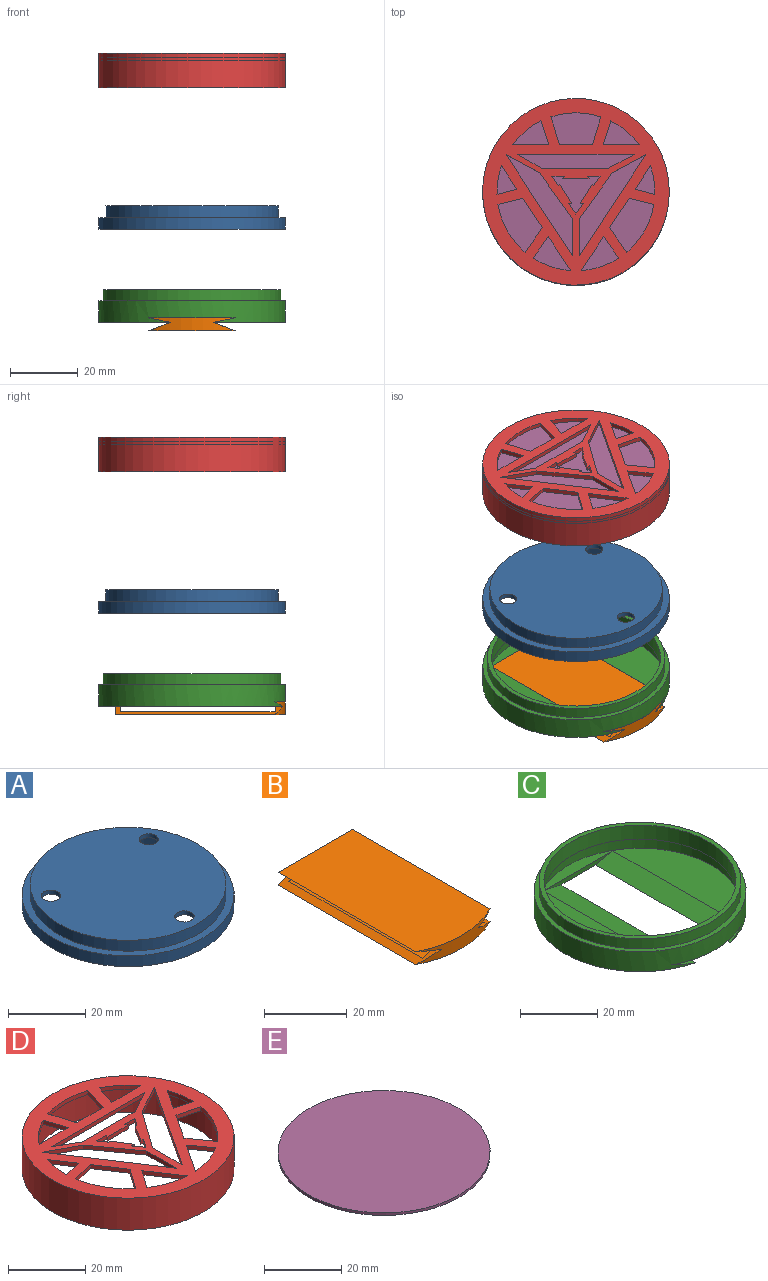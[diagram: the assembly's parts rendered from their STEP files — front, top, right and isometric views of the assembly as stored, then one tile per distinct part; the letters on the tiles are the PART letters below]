
ASSEMBLY  parts=5 mates=4
PART A: 12 faces, bbox 55x55x6.9 mm
  f0: cylinder r=27.5mm len=55mm, axis (0,0,1), area 592.5mm2, adj f1,f2
  f1: plane 55x55mm, normal (0,0,-1), area 214.4mm2, adj f0,f5
  f2: plane 55x55mm, normal (0,0,1), area 349mm2, adj f0,f4
  f3: plane 50.8x50.8mm, normal (0,0,1), area 1967.9mm2, adj f4,f9,f10,f11
  f4: cylinder r=25.4mm len=50.8mm, axis (0,0,1), area 547.2mm2, adj f2,f3
  f5: cylinder r=26.23mm len=52.46mm, axis (0,0,1), area 355.8mm2, adj f1,f6
  f6: plane 52.46x52.46mm, normal (0,0,-1), area 332.2mm2, adj f5,f8
  f7: plane 48.26x48.26mm, normal (0,0,-1), area 1770.3mm2, adj f8,f9,f10,f11
  f8: cylinder r=24.13mm len=48.26mm, axis (0,0,1), area 519.9mm2, adj f6,f7
  f9: cylinder r=2.5mm len=5mm, axis (0,0,-1), area 19.9mm2, adj f3,f7
  f10: cylinder r=2.5mm len=5mm, axis (0,0,-1), area 19.9mm2, adj f3,f7
  f11: cylinder r=2.5mm len=5mm, axis (0,0,-1), area 19.9mm2, adj f3,f7
PART B: 12 faces, bbox 25.4x50.1x3.8 mm
  f0: plane 49.31x6.35mm, normal (-0.37,0,0.93), area 148.6mm2, adj f2,f3,f6,f7,f8,f9,f10,f11
  f1: plane 49.31x6.35mm, normal (0.37,0,0.93), area 148.6mm2, adj f3,f4,f6,f7,f8,f9,f10,f11
  f2: plane 49.31x6.35mm, normal (-0.2,0,-0.98), area 312.6mm2, adj f0,f5,f6,f7
  f3: plane 50.05x25.4mm, normal (0,0,-1), area 1245.6mm2, adj f0,f1,f6,f7
  f4: plane 49.31x6.35mm, normal (0.2,0,-0.98), area 312.6mm2, adj f1,f5,f6,f7
  f5: plane 50.05x25.4mm, normal (0,0,1), area 1245.6mm2, adj f2,f4,f6,f7
  f6: plane 25.4x3.81mm, normal (0,1,0), area 72.6mm2, adj f0,f1,f2,f3,f4,f5
  f7: cylinder r=27.47mm len=25.4mm, axis (0,0,1), area 74.3mm2, adj f0,f1,f2,f3,f4,f5
  f8: plane 21.07x1.48mm, normal (0,-1,0), area 25.7mm2, adj f0,f1,f9,f11
  f9: plane 45.53x13.67mm, normal (0,0,-1), area 622.4mm2, adj f0,f1,f8,f10
  f10: plane 21.07x1.48mm, normal (0,1,0), area 25.7mm2, adj f0,f1,f9,f11
  f11: plane 45.53x21.07mm, normal (0,0,1), area 959.5mm2, adj f0,f1,f8,f10
PART C: 13 faces, bbox 55x55x9.5 mm
  f0: plane 52.41x49.13mm, normal (0,0,1), area 944mm2, adj f6,f9,f10,f11
  f1: cylinder r=27.48mm len=54.95mm, axis (0,0,1), area 1071.4mm2, adj f2,f3,f10,f11,f12
  f2: plane 54.95x54.21mm, normal (0,0,-1), area 1738.3mm2, adj f1,f9,f10,f11
  f3: plane 54.95x54.95mm, normal (0,0,1), area 221.7mm2, adj f1,f5
  f4: plane 52.32x52.32mm, normal (0,0,1), area 203.7mm2, adj f5,f8
  f5: cylinder r=26.16mm len=52.32mm, axis (0,0,1), area 521.9mm2, adj f3,f4
  f6: cylinder r=26.21mm len=52.41mm, axis (0,0,1), area 627.3mm2, adj f0,f7,f12
  f7: plane 52.41x52.41mm, normal (0,0,-1), area 211.2mm2, adj f6,f8
  f8: cylinder r=24.89mm len=49.78mm, axis (0,0,1), area 695.1mm2, adj f4,f7
  f9: plane 25.4x1.27mm, normal (0,-1,0), area 24.2mm2, adj f0,f2,f10,f11
  f10: plane 49.36x6.35mm, normal (0.2,0,0.98), area 313mm2, adj f0,f1,f2,f9,f12
  f11: plane 49.36x6.35mm, normal (-0.2,0,0.98), area 313mm2, adj f0,f1,f2,f9,f12
  f12: plane 25.4x4.55mm, normal (0,0,-1), area 33.6mm2, adj f1,f6,f10,f11
PART D: 62 faces, bbox 55x55x10.2 mm
  f0: plane 55x55mm, normal (0,0,-1), area 349mm2, adj f2,f61
  f1: plane 55x55mm, normal (0,0,1), area 1325.6mm2, adj f2,f3,f4,f5,f6,f7,f8,f9
  f2: cylinder r=27.5mm len=55mm, axis (0,0,-1), area 1755.5mm2, adj f0,f1
  f3: plane 6.92x2.3mm, normal (-0.95,-0.32,0), area 9.3mm2, adj f1,f4,f5,f60
  f4: cylinder r=23.26mm len=8.33mm, axis (0,0,1), area 13.9mm2, adj f1,f3,f5,f60
  f5: plane 10.62x1.27mm, normal (0,1,0), area 13.5mm2, adj f1,f3,f4,f60
  f6: plane 3.04x2.18mm, normal (0.81,0.58,0), area 4.8mm2, adj f1,f7,f20,f60
  f7: plane 3.04x2.18mm, normal (-0.81,0.58,0), area 4.8mm2, adj f1,f6,f8,f60
  f8: plane 1.27x0.97mm, normal (0,-1,0), area 1.2mm2, adj f1,f7,f9,f60
  f9: plane 5.67x3.55mm, normal (-0.85,0.53,0), area 8.5mm2, adj f1,f8,f10,f60
  f10: plane 1.27x0.4mm, normal (0.58,0.81,0), area 0.6mm2, adj f1,f9,f11,f60
  f11: plane 2.71x1.94mm, normal (-0.81,0.58,0), area 4.2mm2, adj f1,f10,f12,f60
  f12: plane 3.69x1.27mm, normal (0,-1,0), area 4.7mm2, adj f1,f11,f13,f60
  f13: plane 1.27x0.82mm, normal (0.88,0.47,0), area 1.2mm2, adj f1,f12,f14,f60
  f14: plane 7.7x1.27mm, normal (0,-1,0), area 9.8mm2, adj f1,f13,f15,f60
  f15: plane 1.27x0.82mm, normal (-0.88,0.47,0), area 1.2mm2, adj f1,f14,f16,f60
  f16: plane 3.69x1.27mm, normal (0,-1,0), area 4.7mm2, adj f1,f15,f17,f60
  f17: plane 2.71x1.94mm, normal (0.81,0.58,0), area 4.2mm2, adj f1,f16,f18,f60
  f18: plane 1.27x0.4mm, normal (-0.58,0.81,0), area 0.6mm2, adj f1,f17,f19,f60
  f19: plane 5.67x3.55mm, normal (0.85,0.53,0), area 8.5mm2, adj f1,f18,f20,f60
  f20: plane 1.27x0.97mm, normal (0,-1,0), area 1.2mm2, adj f1,f6,f19,f60
  f21: plane 8.12x2.48mm, normal (-0.96,0.29,0), area 10.8mm2, adj f1,f22,f24,f60
  f22: cylinder r=23.26mm len=14.72mm, axis (0,0,1), area 19mm2, adj f1,f21,f23,f60
  f23: plane 8.12x2.48mm, normal (0.96,0.29,0), area 10.8mm2, adj f1,f22,f24,f60
  f24: plane 9.76x1.27mm, normal (0,1,0), area 12.4mm2, adj f1,f21,f23,f60
  f25: plane 6.92x2.3mm, normal (0.95,-0.32,0), area 9.3mm2, adj f1,f26,f27,f60
  f26: plane 10.62x1.27mm, normal (0,1,0), area 13.5mm2, adj f1,f25,f27,f60
  f27: cylinder r=23.26mm len=8.33mm, axis (0,0,1), area 13.9mm2, adj f1,f25,f26,f60
  f28: cylinder r=23.26mm len=8.41mm, axis (0,0,1), area 10.9mm2, adj f1,f29,f30,f60
  f29: plane 6.87x4.55mm, normal (0.83,-0.55,0), area 10.5mm2, adj f1,f28,f30,f60
  f30: plane 5.82x1.55mm, normal (0.26,0.97,0), area 7.7mm2, adj f1,f28,f29,f60
  f31: plane 7.19x5.09mm, normal (0.82,0.58,0), area 11.2mm2, adj f1,f32,f34,f60
  f32: cylinder r=23.26mm len=14.08mm, axis (0,0,1), area 21mm2, adj f1,f31,f33,f60
  f33: plane 7.31x1.83mm, normal (-0.24,-0.97,0), area 9.6mm2, adj f1,f32,f34,f60
  f34: plane 8.71x5.77mm, normal (0.83,-0.55,0), area 13.3mm2, adj f1,f31,f33,f60
  f35: plane 6.87x4.55mm, normal (-0.83,-0.55,0), area 10.5mm2, adj f1,f36,f37,f60
  f36: cylinder r=23.26mm len=8.41mm, axis (0,0,1), area 10.9mm2, adj f1,f35,f37,f60
  f37: plane 5.82x1.55mm, normal (-0.26,0.97,0), area 7.7mm2, adj f1,f35,f36,f60
  f38: plane 7.31x1.83mm, normal (0.24,-0.97,0), area 9.6mm2, adj f1,f39,f41,f60
  f39: cylinder r=23.26mm len=14.08mm, axis (0,0,1), area 21mm2, adj f1,f38,f40,f60
  f40: plane 7.19x5.09mm, normal (-0.82,0.58,0), area 11.2mm2, adj f1,f39,f41,f60
  f41: plane 8.71x5.77mm, normal (-0.83,-0.55,0), area 13.3mm2, adj f1,f38,f40,f60
  f42: plane 6.29x4.49mm, normal (0.81,-0.58,0), area 9.8mm2, adj f1,f43,f44,f60
  f43: cylinder r=23.26mm len=11.09mm, axis (0,0,1), area 15mm2, adj f1,f42,f44,f60
  f44: plane 9.96x6.6mm, normal (-0.83,-0.55,0), area 15.2mm2, adj f1,f42,f43,f60
  f45: plane 9.96x6.6mm, normal (0.83,-0.55,0), area 15.2mm2, adj f1,f46,f47,f60
  f46: cylinder r=23.26mm len=11.09mm, axis (0,0,1), area 15mm2, adj f1,f45,f47,f60
  f47: plane 6.29x4.49mm, normal (-0.81,-0.58,0), area 9.8mm2, adj f1,f45,f46,f60
  f48: plane 19.3x1.27mm, normal (0,1,0), area 24.5mm2, adj f1,f49,f51,f60
  f49: plane 7.79x4.2mm, normal (-0.47,0.88,0), area 11.2mm2, adj f1,f48,f50,f60
  f50: plane 34.4x1.27mm, normal (0,-1,0), area 43.7mm2, adj f1,f49,f51,f60
  f51: plane 7.31x4.2mm, normal (0.5,0.87,0), area 10.7mm2, adj f1,f48,f50,f60
  f52: plane 29.72x19.52mm, normal (0.84,0.55,0), area 45.2mm2, adj f1,f53,f55,f60
  f53: plane 10.91x1.27mm, normal (-1,0,0), area 13.9mm2, adj f1,f52,f54,f60
  f54: plane 13.55x9.71mm, normal (-0.81,-0.58,0), area 21.2mm2, adj f1,f53,f55,f60
  f55: plane 9.81x5.27mm, normal (-0.47,-0.88,0), area 14.1mm2, adj f1,f52,f54,f60
  f56: plane 10.91x1.27mm, normal (1,0,0), area 13.9mm2, adj f1,f57,f59,f60
  f57: plane 29.72x19.52mm, normal (-0.84,0.55,0), area 45.2mm2, adj f1,f56,f58,f60
  f58: plane 9.81x5.27mm, normal (0.47,-0.88,0), area 14.1mm2, adj f1,f57,f59,f60
  f59: plane 13.55x9.71mm, normal (0.81,-0.58,0), area 21.2mm2, adj f1,f56,f58,f60
  f60: plane 50.8x50.8mm, normal (0,0,-1), area 976.6mm2, adj f3,f4,f5,f6,f7,f8,f9,f10
  f61: cylinder r=25.4mm len=50.8mm, axis (0,0,-1), area 1418.8mm2, adj f0,f60
PART E: 3 faces, bbox 55x55x0.8 mm
  f0: cylinder r=27.5mm len=54.99mm, axis (0,0,-1), area 137.1mm2, adj f1,f2
  f1: plane 54.99x54.99mm, normal (0,0,1), area 2375.1mm2, adj f0
  f2: plane 54.99x54.99mm, normal (0,0,-1), area 2375.1mm2, adj f0
PLACE A t=(0,0,3.43)mm
PLACE B t=(0,0.05,-21.09)mm
PLACE C t=(0,0,-21.09)mm
PLACE D t=(0,0,41.7)mm
PLACE E t=(0,0,49.8)mm
MATE slider A.f4 <-> D.f2  axis (0,0,1) through (0,0,6.86)mm
MATE slider A.f4 <-> C.f1  axis (0,0,-1) through (0,0,5.59)mm
MATE fastened E.f0 <-> D.f4  axis (0,0,1) through (0,0,50.59)mm
MATE fastened B.f6 <-> C.f9  axis (0,1,0) through (0,22.63,-26.17)mm
